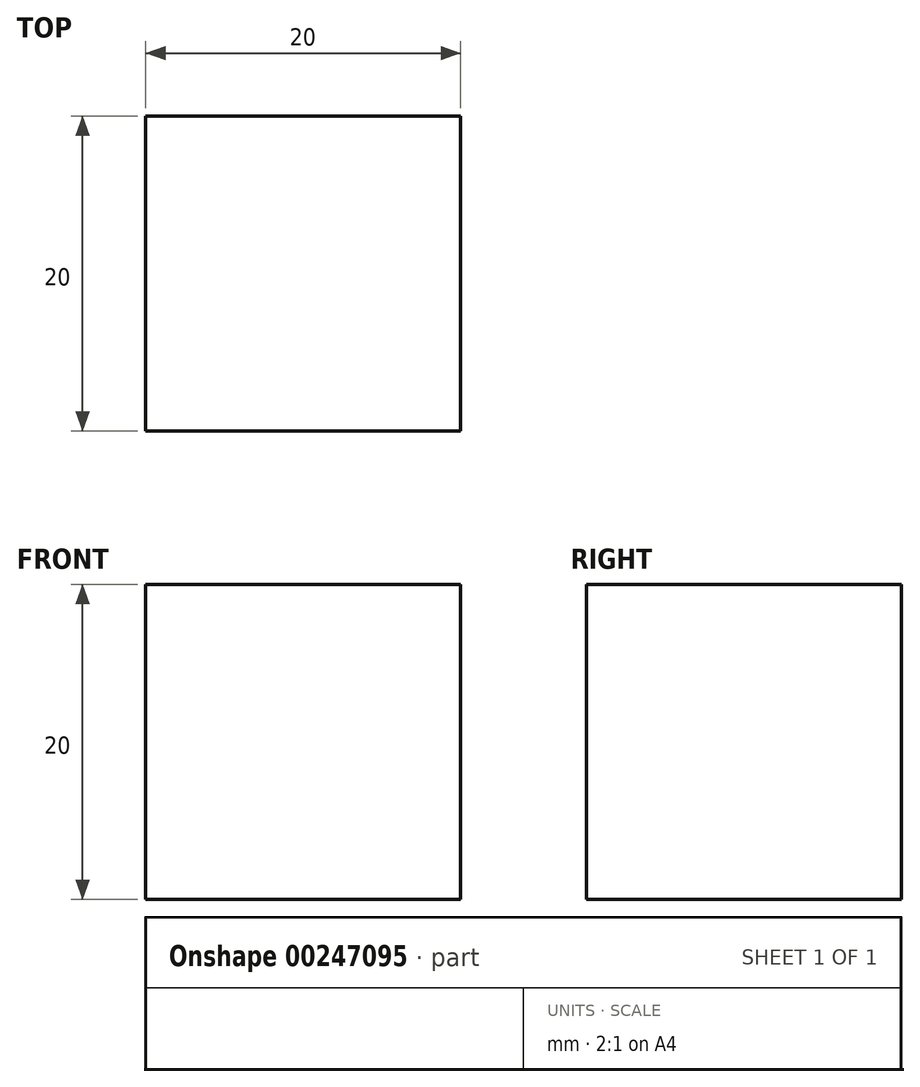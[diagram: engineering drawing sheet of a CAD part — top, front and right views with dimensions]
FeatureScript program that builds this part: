
annotation { "Feature Type Name" : "Feature", "Feature Type Description" : "" }
export const myFeature = defineFeature(function(context is Context, id is Id, definition is map)
    precondition{}
    {
        {
            var Q0;
            Q0=qCreatedBy(makeId("Top.planeOp"),FACE);
            var sketch = newSketch(context, id + "F0", { "sketchPlane" : qUnion([Q0])});
            skLineSegment(sketch, "E0.bottom", {"start": v(0, 0) * mm, "end": v(20, 0) * mm});
            skLineSegment(sketch, "E0.top", {"start": v(0, 20) * mm, "end": v(20, 20) * mm});
            skLineSegment(sketch, "E0.left", {"start": v(0, 0) * mm, "end": v(0, 20) * mm});
            skLineSegment(sketch, "E0.right", {"start": v(20, 0) * mm, "end": v(20, 20) * mm});
            skSolve(sketch);
        }
        {
            var Q0;
            Q0=makeQuery(id+"F0.imprint","IMPRINT",FACE,{"disambiguationData":[TD([[makeQuery(id+"F0.imprint","IMPRINT",EDGE,{"derivedFrom":sQuery(id+"F0.wireOp",EDGE,"E0.bottom")}),1.0]])]});
            extrude(context, id + "F1", {"entities" : qUnion([Q0]), "depth" : 20 * mm, "offsetDistance" : 25 * mm});
        }
    });
